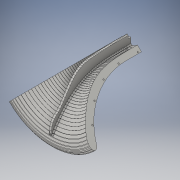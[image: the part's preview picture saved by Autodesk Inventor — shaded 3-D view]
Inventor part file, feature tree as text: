
AUTODESK INVENTOR PART (.ipt)
format: ipt  version: 2016 SP1 (Build 200210100, 210)  size: 3,855,872 bytes
history: native  units: in
note: dims shown in document units (in); Inventor stores cm internally (conversion verified against a paired STEP export)
features: hole x1, sketch x1, other x1
ambient origin geometry x8: Origin, YZ Plane, XZ Plane, XY Plane, X Axis, Y Axis, Z Axis, Center Point
bodies: Solid1 (feature_tree)
feature tree (3):
  hole  "Hole1"  [1 undecoded]
  sketch  "Sketch1"  dims[d0=0.516in d1=0.171in d2=0.432in d3=0.375in d4=0.25in d5=0.5635in d6=0.64in d7=0.8108in]
  parser-record x1  (decoder bookkeeping rows leaked as tree rows — omitted from the tree; the rows remain in map.json)
note: 1 required parameter value undecoded (feature->parameter linkage not recoverable at this tier; creation-order binding heuristic only, values carry confidence <= 0.55)
